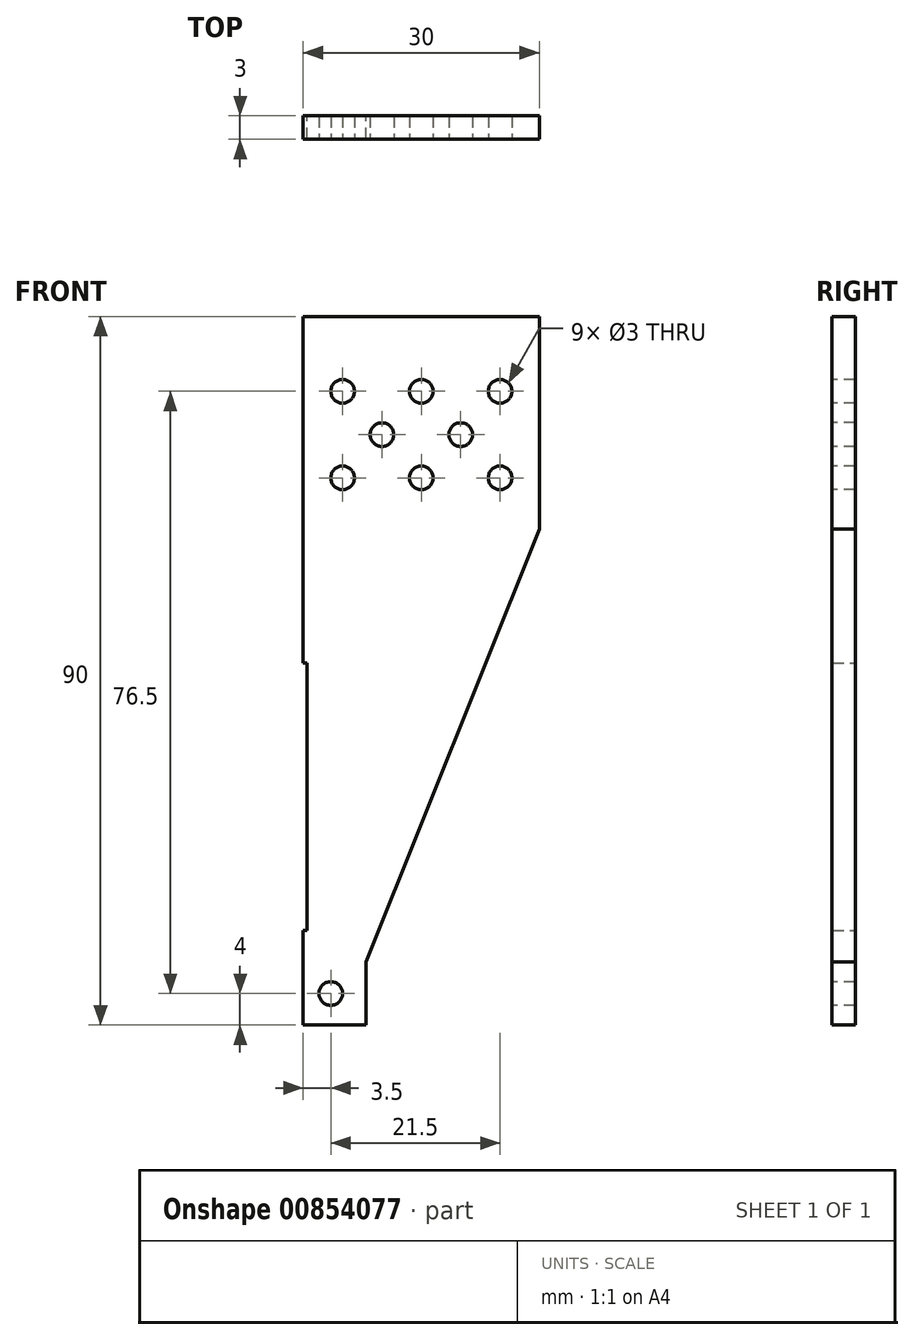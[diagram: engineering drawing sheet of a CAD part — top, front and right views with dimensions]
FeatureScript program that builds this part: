
annotation { "Feature Type Name" : "Feature", "Feature Type Description" : "" }
export const myFeature = defineFeature(function(context is Context, id is Id, definition is map)
    precondition{}
    {
        {
            var Q0;
            Q0=qCreatedBy(makeId("Front.planeOp"),FACE);
            var sketch = newSketch(context, id + "F0", { "sketchPlane" : qUnion([Q0])});
            skLineSegment(sketch, "E0", {"start": v(0, 0) * mm, "end": v(8, 0) * mm});
            skLineSegment(sketch, "E1", {"start": v(8, 0) * mm, "end": v(8, 8) * mm});
            skLineSegment(sketch, "E2", {"start": v(8, 8) * mm, "end": v(30, 63) * mm});
            skLineSegment(sketch, "E3", {"start": v(30, 63) * mm, "end": v(30, 90) * mm});
            skLineSegment(sketch, "E4", {"start": v(30, 90) * mm, "end": v(0, 90) * mm});
            skLineSegment(sketch, "E5", {"start": v(0, 90) * mm, "end": v(0, 46) * mm});
            skLineSegment(sketch, "E6", {"start": v(0, 46) * mm, "end": v(0.5, 46) * mm});
            skLineSegment(sketch, "E7", {"start": v(0.5, 46) * mm, "end": v(0.5, 12) * mm});
            skLineSegment(sketch, "E8", {"start": v(0.5, 12) * mm, "end": v(0, 12) * mm});
            skLineSegment(sketch, "E9", {"start": v(0, 12) * mm, "end": v(0, 0) * mm});
            skSolve(sketch);
        }
        {
            var Q0;
            Q0=makeQuery(id+"F0.imprint","IMPRINT",FACE,{"disambiguationData":[TD([[makeQuery(id+"F0.imprint","IMPRINT",EDGE,{"derivedFrom":sQuery(id+"F0.wireOp",EDGE,"E0")}),1.0]])]});
            extrude(context, id + "F1", {"entities" : qUnion([Q0]), "flatOperationType" : FlatOperationType.REMOVE, "depth" : 3 * mm, "offsetDistance" : 25 * mm, "domain" : OperationDomain.MODEL});
        }
        {
            var Q0;
            Q0=qCreatedBy(makeId("Front.planeOp"),FACE);
            var sketch = newSketch(context, id + "F2", { "sketchPlane" : qUnion([Q0])});
            skPoint(sketch, "E10", {"position": v(5, 80.5) * mm});
            skPoint(sketch, "E11", {"position": v(15, 80.5) * mm});
            skPoint(sketch, "E12", {"position": v(25, 80.5) * mm});
            skPoint(sketch, "E13", {"position": v(10, 75) * mm});
            skPoint(sketch, "E14", {"position": v(20, 75) * mm});
            skPoint(sketch, "E15", {"position": v(5, 69.5) * mm});
            skPoint(sketch, "E16", {"position": v(15, 69.5) * mm});
            skPoint(sketch, "E17", {"position": v(25, 69.5) * mm});
            skPoint(sketch, "E18", {"position": v(3.5, 4) * mm});
            skSolve(sketch);
        }
        {
            var Q0;
            Q0=sQuery(id+"F2.wireOp",VERTEX,"E10");
            var Q1;
            Q1=sQuery(id+"F2.wireOp",VERTEX,"E11");
            var Q2;
            Q2=sQuery(id+"F2.wireOp",VERTEX,"E12");
            var Q3;
            Q3=sQuery(id+"F2.wireOp",VERTEX,"E14");
            var Q4;
            Q4=sQuery(id+"F2.wireOp",VERTEX,"E13");
            var Q5;
            Q5=sQuery(id+"F2.wireOp",VERTEX,"E15");
            var Q6;
            Q6=sQuery(id+"F2.wireOp",VERTEX,"E17");
            var Q7;
            Q7=sQuery(id+"F2.wireOp",VERTEX,"E16");
            var Q8;
            Q8=sQuery(id+"F2.wireOp",VERTEX,"E18");
            var Q9;
            Q9=makeQuery(id+"F1.opExtrude","SWEPT_BODY",BODY,{"disambiguationData":[OSD([sQuery(id+"F0.wireOp",EDGE,"E0"),sQuery(id+"F0.wireOp",EDGE,"E1"),sQuery(id+"F0.wireOp",EDGE,"E2"),sQuery(id+"F0.wireOp",EDGE,"E3"),sQuery(id+"F0.wireOp",EDGE,"E4"),sQuery(id+"F0.wireOp",EDGE,"E5"),sQuery(id+"F0.wireOp",EDGE,"E6"),sQuery(id+"F0.wireOp",EDGE,"E7"),sQuery(id+"F0.wireOp",EDGE,"E8"),sQuery(id+"F0.wireOp",EDGE,"E9")])]});
            hole(context, id + "F3", {"style" : HoleStyle.SIMPLE, "endStyle" : HoleEndStyle.THROUGH, "oppositeDirection" : true, "holeDiameter" : 3 * mm, "majorDiameter" : 5 * mm, "isTappedThrough" : true, "tappedDepth" : 12 * mm, "tapClearance" : 3, "locations" : qUnion([Q0, Q1, Q2, Q3, Q4, Q5, Q6, Q7, Q8]), "scope" : qUnion([Q9]), "startStyle" : HoleStartStyle.SKETCH});
        }
    });
